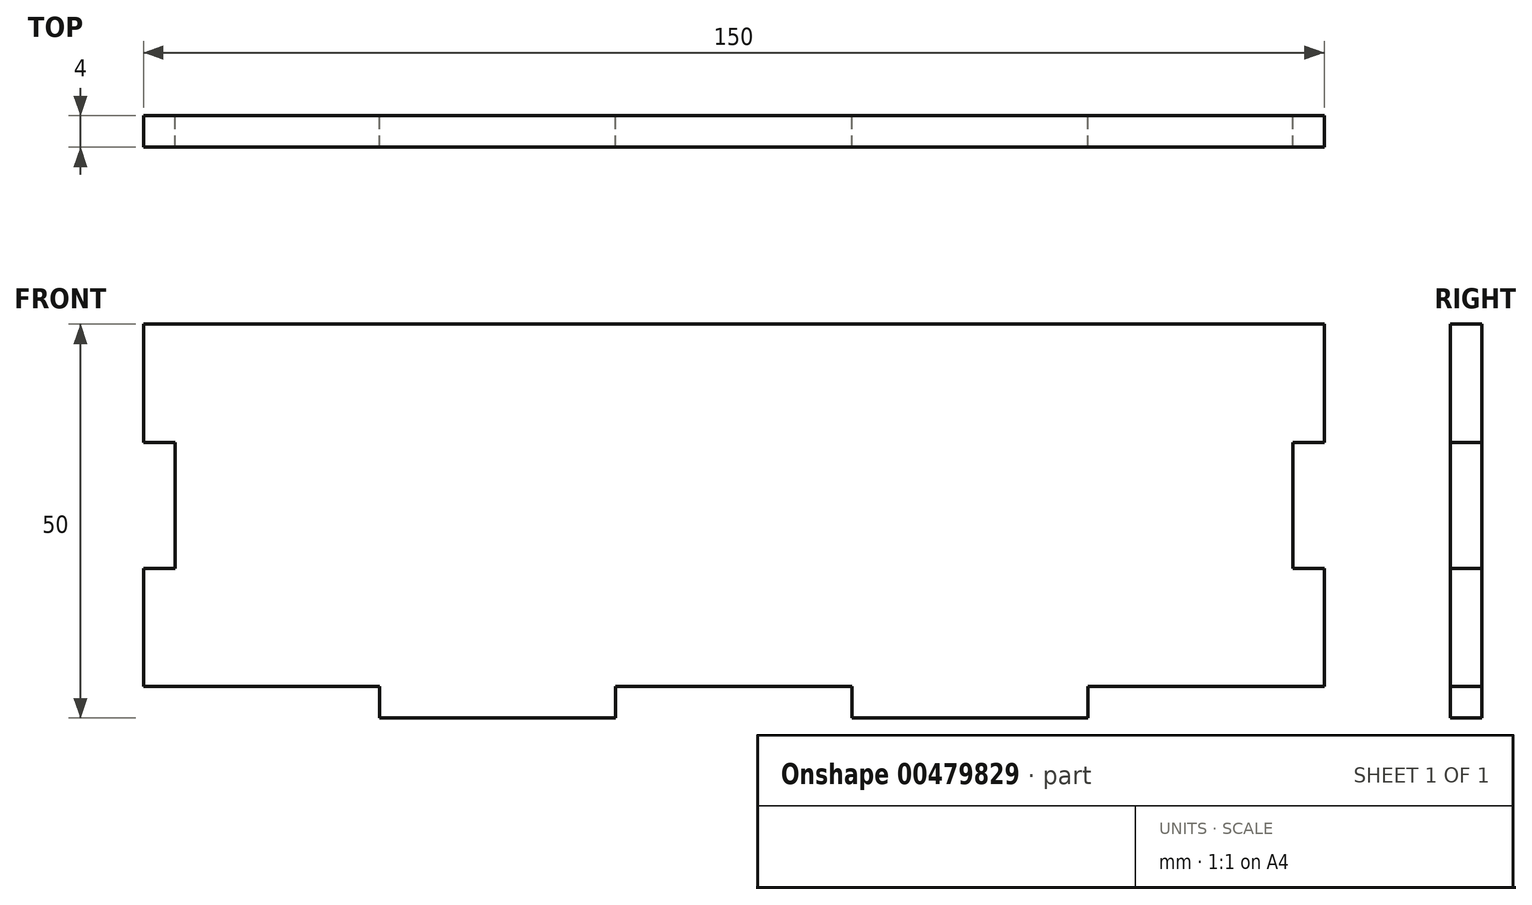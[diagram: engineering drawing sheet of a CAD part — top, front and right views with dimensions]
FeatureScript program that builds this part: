
annotation { "Feature Type Name" : "Feature", "Feature Type Description" : "" }
export const myFeature = defineFeature(function(context is Context, id is Id, definition is map)
    precondition{}
    {
        {
            var Q0;
            Q0=qCreatedBy(makeId("Front.planeOp"),FACE);
            var sketch = newSketch(context, id + "F0", { "sketchPlane" : qUnion([Q0])});
            skLineSegment(sketch, "E0.bottom", {"start": v(0, 0) * mm, "end": v(150, 0) * mm});
            skLineSegment(sketch, "E0.top", {"start": v(0, 50) * mm, "end": v(150, 50) * mm});
            skLineSegment(sketch, "E0.left", {"start": v(0, 0) * mm, "end": v(0, 50) * mm});
            skLineSegment(sketch, "E0.right", {"start": v(150, 0) * mm, "end": v(150, 50) * mm});
            skLineSegment(sketch, "E1.bottom", {"start": v(0, 0) * mm, "end": v(30, 0) * mm});
            skLineSegment(sketch, "E1.top", {"start": v(0, 4) * mm, "end": v(30, 4) * mm});
            skLineSegment(sketch, "E1.left", {"start": v(0, 0) * mm, "end": v(0, 4) * mm});
            skLineSegment(sketch, "E1.right", {"start": v(30, 0) * mm, "end": v(30, 4) * mm});
            skLineSegment(sketch, "E2.bottom", {"start": v(150, 0) * mm, "end": v(120, 0) * mm});
            skLineSegment(sketch, "E2.top", {"start": v(150, 4) * mm, "end": v(120, 4) * mm});
            skLineSegment(sketch, "E2.left", {"start": v(150, 0) * mm, "end": v(150, 4) * mm});
            skLineSegment(sketch, "E2.right", {"start": v(120, 0) * mm, "end": v(120, 4) * mm});
            skLineSegment(sketch, "E3.bottom", {"start": v(90, 0) * mm, "end": v(60, 0) * mm});
            skLineSegment(sketch, "E3.top", {"start": v(90, 4) * mm, "end": v(60, 4) * mm});
            skLineSegment(sketch, "E3.left", {"start": v(90, 0) * mm, "end": v(90, 4) * mm});
            skLineSegment(sketch, "E3.right", {"start": v(60, 0) * mm, "end": v(60, 4) * mm});
            skLineSegment(sketch, "E4.bottom", {"start": v(0, 35) * mm, "end": v(4, 35) * mm});
            skLineSegment(sketch, "E4.top", {"start": v(0, 19) * mm, "end": v(4, 19) * mm});
            skLineSegment(sketch, "E4.left", {"start": v(0, 35) * mm, "end": v(0, 19) * mm});
            skLineSegment(sketch, "E4.right", {"start": v(4, 35) * mm, "end": v(4, 19) * mm});
            skLineSegment(sketch, "E5.bottom", {"start": v(150, 35) * mm, "end": v(146, 35) * mm});
            skLineSegment(sketch, "E5.top", {"start": v(150, 19) * mm, "end": v(146, 19) * mm});
            skLineSegment(sketch, "E5.left", {"start": v(150, 35) * mm, "end": v(150, 19) * mm});
            skLineSegment(sketch, "E5.right", {"start": v(146, 35) * mm, "end": v(146, 19) * mm});
            skSolve(sketch);
        }
        {
            var Q0;
            {var subQ3=sQuery(id+"F0.wireOp",EDGE,"E0.top");Q0=makeQuery(id+"F0.imprint","IMPRINT",FACE,{"disambiguationData":[TD([[makeQuery(id+"F0.imprint","IMPRINT",EDGE,{"derivedFrom":subQ3}),-1.0]])]});}
            extrude(context, id + "F1", {"entities" : qUnion([Q0]), "depth" : 4 * mm});
        }
    });
